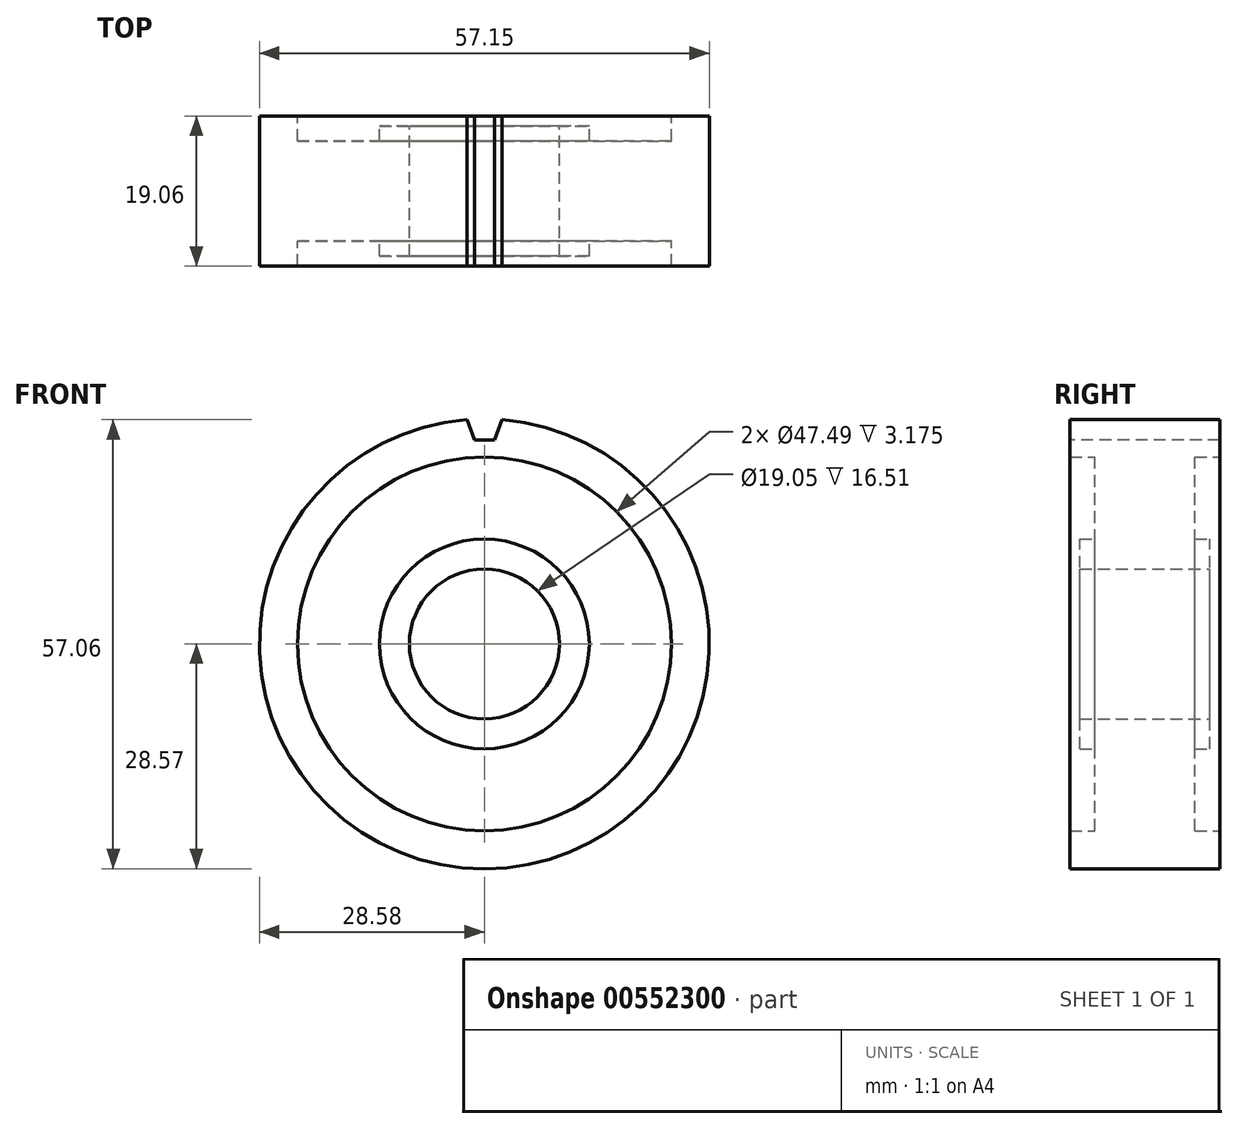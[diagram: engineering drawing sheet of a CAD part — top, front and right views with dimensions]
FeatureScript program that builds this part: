
annotation { "Feature Type Name" : "Feature", "Feature Type Description" : "" }
export const myFeature = defineFeature(function(context is Context, id is Id, definition is map)
    precondition{}
    {
        {
            var Q0;
            Q0=qCreatedBy(makeId("Front.planeOp"),FACE);
            var sketch = newSketch(context, id + "F0", { "sketchPlane" : qUnion([Q0])});
            skCircle(sketch, "E0", {"center": v(0, 0) * mm, "radius": 28.58 * mm});
            skCircle(sketch, "E1", {"center": v(0, 0) * mm, "radius": 9.53 * mm});
            skCircle(sketch, "E2", {"center": v(0, 0) * mm, "radius": 13.32 * mm});
            skCircle(sketch, "E3", {"center": v(0, 0) * mm, "radius": 25.92 * mm});
            skCircle(sketch, "E4", {"center": v(0, 0) * mm, "radius": 23.75 * mm});
            skLineSegment(sketch, "E5", {"start": v(1.27, 25.89) * mm, "end": v(2.22, 28.49) * mm});
            skLineSegment(sketch, "E6", {"start": v(-1.27, 25.89) * mm, "end": v(-2.22, 28.49) * mm});
            skSolve(sketch);
        }
        {
            var Q0;
            Q0=makeQuery(id+"F0.imprint","IMPRINT",FACE,{"disambiguationData":[TD([[makeQuery(id+"F0.imprint","IMPRINT",EDGE,{"derivedFrom":sQuery(id+"F0.wireOp",EDGE,"E2")}),-1.0]])]});
            extrude(context, id + "F1", {"entities" : qUnion([Q0]), "endBound" : BoundingType.SYMMETRIC, "depth" : 12.7 * mm, "offsetDistance" : 25.4 * mm});
        }
        {
            var Q0;
            Q0=makeQuery(id+"F0.imprint","IMPRINT",FACE,{"disambiguationData":[TD([[makeQuery(id+"F0.imprint","IMPRINT",EDGE,{"derivedFrom":sQuery(id+"F0.wireOp",EDGE,"E4")}),-1.0]])]});
            var Q1;
            {var subQ0=sQuery(id+"F0.wireOp",EDGE,"hvfpBGEB-Zu3b-O9fP-W4ZX-r0UMkodEAVbn");Q1=makeQuery(id+"F0.imprint","IMPRINT",FACE,{"disambiguationData":[TD([[makeQuery(id+"F0.imprint","IMPRINT",EDGE,{"derivedFrom":subQ0}),1.0]])]});}
            var Q2;
            {var subQ0=sQuery(id+"F0.wireOp",EDGE,"hvfpBGEB-Zu3b-O9fP-W4ZX-r0UMkodEAVbn");Q2=makeQuery(id+"F0.imprint","IMPRINT",FACE,{"disambiguationData":[TD([[makeQuery(id+"F0.imprint","IMPRINT",EDGE,{"derivedFrom":subQ0}),-1.0]])]});}
            extrude(context, id + "F2", {"entities" : qUnion([Q0, Q1, Q2]), "operationType" : NewBodyOperationType.ADD, "endBound" : BoundingType.SYMMETRIC, "depth" : 19.05 * mm, "offsetDistance" : 25.4 * mm});
        }
        {
            var Q0;
            Q0=makeQuery(id+"F0.imprint","IMPRINT",FACE,{"disambiguationData":[TD([[makeQuery(id+"F0.imprint","IMPRINT",EDGE,{"derivedFrom":sQuery(id+"F0.wireOp",EDGE,"E1")}),-1.0]])]});
            extrude(context, id + "F3", {"entities" : qUnion([Q0]), "operationType" : NewBodyOperationType.ADD, "endBound" : BoundingType.SYMMETRIC, "depth" : 16.5 * mm, "offsetDistance" : 25.4 * mm});
        }
        {
            var Q0;
            {var subQ0=sQuery(id+"F0.wireOp",EDGE,"E5");Q0=makeQuery(id+"F0.imprint","IMPRINT",FACE,{"disambiguationData":[TD([[makeQuery(id+"F0.imprint","IMPRINT",EDGE,{"derivedFrom":subQ0}),1.0]])]});}
            var Q1;
            {var subQ0=sQuery(id+"F0.wireOp",EDGE,"E5");Q1=makeQuery(id+"F0.imprint","IMPRINT",FACE,{"disambiguationData":[TD([[makeQuery(id+"F0.imprint","IMPRINT",EDGE,{"derivedFrom":subQ0}),-1.0]])]});}
            extrude(context, id + "F4", {"entities" : qUnion([Q0, Q1]), "operationType" : NewBodyOperationType.ADD, "endBound" : BoundingType.SYMMETRIC, "depth" : 19.05 * mm, "offsetDistance" : 25.4 * mm});
        }
        {
            var Q0;
            {var subQ0=sQuery(id+"F0.wireOp",EDGE,"E5");Q0=makeQuery(id+"F0.imprint","IMPRINT",FACE,{"disambiguationData":[TD([[makeQuery(id+"F0.imprint","IMPRINT",EDGE,{"derivedFrom":subQ0}),1.0]])]});}
            extrude(context, id + "F5", {"entities" : qUnion([Q0]), "operationType" : NewBodyOperationType.REMOVE, "endBound" : BoundingType.SYMMETRIC, "oppositeDirection" : true, "depth" : 19.05 * mm, "offsetDistance" : 25.4 * mm});
        }
    });
